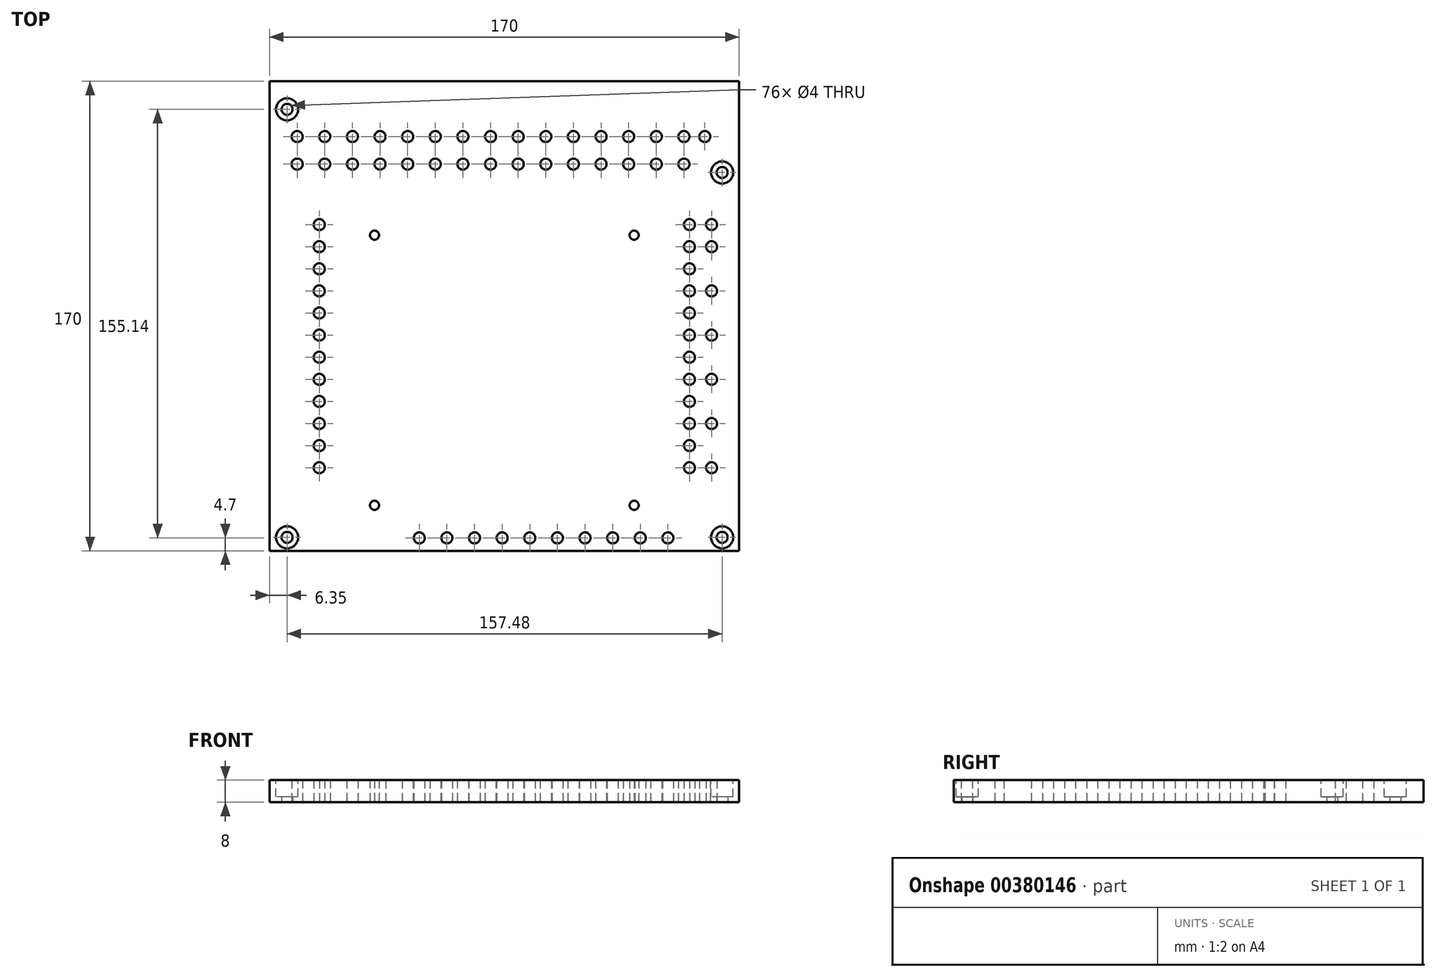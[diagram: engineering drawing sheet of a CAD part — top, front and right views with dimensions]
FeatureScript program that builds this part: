
annotation { "Feature Type Name" : "Feature", "Feature Type Description" : "" }
export const myFeature = defineFeature(function(context is Context, id is Id, definition is map)
    precondition{}
    {
        {
            var Q0;
            Q0=qCreatedBy(makeId("Top.planeOp"),FACE);
            var sketch = newSketch(context, id + "F0", { "sketchPlane" : qUnion([Q0])});
            skLineSegment(sketch, "E0.bottom", {"start": v(0, 0) * mm, "end": v(170, 0) * mm});
            skLineSegment(sketch, "E0.top", {"start": v(0, -170) * mm, "end": v(170, -170) * mm});
            skLineSegment(sketch, "E0.left", {"start": v(0, 0) * mm, "end": v(0, -170) * mm});
            skLineSegment(sketch, "E0.right", {"start": v(170, 0) * mm, "end": v(170, -170) * mm});
            skCircle(sketch, "E1", {"center": v(6.35, -10.16) * mm, "radius": 2 * mm});
            skCircle(sketch, "E2", {"center": v(163.83, -165.1) * mm, "radius": 2 * mm});
            skCircle(sketch, "E3", {"center": v(6.35, -165.1) * mm, "radius": 2 * mm});
            skCircle(sketch, "E4", {"center": v(163.83, -33.02) * mm, "radius": 2 * mm});
            skLineSegment(sketch, "E5.bottom", {"start": v(34.2, -51.9) * mm, "end": v(135.8, -51.9) * mm, "construction": true});
            skLineSegment(sketch, "E5.top", {"start": v(34.2, -157.3) * mm, "end": v(135.8, -157.3) * mm, "construction": true});
            skLineSegment(sketch, "E5.left", {"start": v(34.2, -51.89) * mm, "end": v(34.2, -157.3) * mm, "construction": true});
            skLineSegment(sketch, "E5.right", {"start": v(135.8, -51.89) * mm, "end": v(135.8, -157.3) * mm, "construction": true});
            skCircle(sketch, "E6", {"center": v(38, -55.7) * mm, "radius": 1.65 * mm});
            skLineSegment(sketch, "E7", {"start": v(85, -51.89) * mm, "end": v(85, -73.54) * mm, "construction": true});
            skLineSegment(sketch, "E8", {"start": v(34.2, -104.6) * mm, "end": v(74.49, -104.6) * mm, "construction": true});
            skCircle(sketch, "E9.MirrorC", {"center": v(38.01, -153.5) * mm, "radius": 1.65 * mm});
            skCircle(sketch, "E10.MirrorC", {"center": v(132, -55.7) * mm, "radius": 1.65 * mm});
            skCircle(sketch, "E11.MirrorC", {"center": v(132, -153.5) * mm, "radius": 1.65 * mm});
            skLineSegment(sketch, "E12", {"start": v(0, -85) * mm, "end": v(12.23, -85) * mm, "construction": true});
            skLineSegment(sketch, "E13", {"start": v(85, -170) * mm, "end": v(85, -151.97) * mm, "construction": true});
            skText(sketch, "E14", { "text": "Motors", "fontName": "OpenSans-Regular.ttf"});
            skText(sketch, "E15", { "text": "backside", "fontName": "OpenSans-Regular.ttf"});
            skText(sketch, "E16", { "text": "limit switches\n", "fontName": "OpenSans-Regular.ttf"});
            skLineSegment(sketch, "E17", {"start": v(18, -51.89) * mm, "end": v(18, -125.95) * mm, "construction": true});
            skCircle(sketch, "E18", {"center": v(18, -51.89) * mm, "radius": 2 * mm});
            skText(sketch, "E19", { "text": "USB", "fontName": "OpenSans-Regular.ttf"});
            skText(sketch, "E20", { "text": "24V", "fontName": "OpenSans-Regular.ttf"});
            skCircle(sketch, "E21.0.1.0", {"center": v(18, -59.89) * mm, "radius": 2 * mm});
            skCircle(sketch, "E21.0.2.0", {"center": v(18, -67.89) * mm, "radius": 2 * mm});
            skCircle(sketch, "E21.0.3.0", {"center": v(18, -75.89) * mm, "radius": 2 * mm});
            skCircle(sketch, "E21.0.4.0", {"center": v(18, -83.89) * mm, "radius": 2 * mm});
            skCircle(sketch, "E21.0.5.0", {"center": v(18, -91.89) * mm, "radius": 2 * mm});
            skCircle(sketch, "E21.0.6.0", {"center": v(18, -99.89) * mm, "radius": 2 * mm});
            skCircle(sketch, "E21.0.7.0", {"center": v(18, -107.89) * mm, "radius": 2 * mm});
            skLineSegment(sketch, "E21.direction1", {"start": v(18, -51.9) * mm, "end": v(9.88, -51.9) * mm, "construction": true});
            skLineSegment(sketch, "E21.direction2", {"start": v(18, -51.89) * mm, "end": v(18, -59.89) * mm, "construction": true});
            skCircle(sketch, "E22.0.0.8", {"center": v(18, -115.89) * mm, "radius": 2 * mm});
            skCircle(sketch, "E22.0.0.9", {"center": v(18, -123.89) * mm, "radius": 2 * mm});
            skCircle(sketch, "E22.0.0.10", {"center": v(18, -131.89) * mm, "radius": 2 * mm});
            skCircle(sketch, "E22.0.0.11", {"center": v(18, -139.89) * mm, "radius": 2 * mm});
            skCircle(sketch, "E23", {"center": v(10, -20) * mm, "radius": 2 * mm});
            skCircle(sketch, "E24.14.0.0", {"center": v(157.56, -20) * mm, "radius": 2 * mm});
            skCircle(sketch, "E25.0.1.0", {"center": v(10, -30) * mm, "radius": 2 * mm});
            skCircle(sketch, "E25.1.0.0", {"center": v(20, -20) * mm, "radius": 2 * mm});
            skCircle(sketch, "E25.1.1.0", {"center": v(20, -30) * mm, "radius": 2 * mm});
            skCircle(sketch, "E25.2.0.0", {"center": v(30, -20) * mm, "radius": 2 * mm});
            skCircle(sketch, "E25.2.1.0", {"center": v(30, -30) * mm, "radius": 2 * mm});
            skCircle(sketch, "E25.3.0.0", {"center": v(40, -20) * mm, "radius": 2 * mm});
            skCircle(sketch, "E25.3.1.0", {"center": v(40, -30) * mm, "radius": 2 * mm});
            skCircle(sketch, "E25.4.0.0", {"center": v(50, -20) * mm, "radius": 2 * mm});
            skCircle(sketch, "E25.4.1.0", {"center": v(50, -30) * mm, "radius": 2 * mm});
            skCircle(sketch, "E25.5.0.0", {"center": v(60, -20) * mm, "radius": 2 * mm});
            skCircle(sketch, "E25.5.1.0", {"center": v(60, -30) * mm, "radius": 2 * mm});
            skCircle(sketch, "E25.6.0.0", {"center": v(70, -20) * mm, "radius": 2 * mm});
            skCircle(sketch, "E25.6.1.0", {"center": v(70, -30) * mm, "radius": 2 * mm});
            skCircle(sketch, "E25.7.0.0", {"center": v(80, -20) * mm, "radius": 2 * mm});
            skCircle(sketch, "E25.7.1.0", {"center": v(80, -30) * mm, "radius": 2 * mm});
            skCircle(sketch, "E25.8.0.0", {"center": v(90, -20) * mm, "radius": 2 * mm});
            skCircle(sketch, "E25.8.1.0", {"center": v(90, -30) * mm, "radius": 2 * mm});
            skCircle(sketch, "E25.9.0.0", {"center": v(100, -20) * mm, "radius": 2 * mm});
            skCircle(sketch, "E25.9.1.0", {"center": v(100, -30) * mm, "radius": 2 * mm});
            skCircle(sketch, "E25.10.0.0", {"center": v(110, -20) * mm, "radius": 2 * mm});
            skCircle(sketch, "E25.10.1.0", {"center": v(110, -30) * mm, "radius": 2 * mm});
            skCircle(sketch, "E25.11.0.0", {"center": v(120, -20) * mm, "radius": 2 * mm});
            skCircle(sketch, "E25.11.1.0", {"center": v(120, -30) * mm, "radius": 2 * mm});
            skCircle(sketch, "E25.12.0.0", {"center": v(130, -20) * mm, "radius": 2 * mm});
            skCircle(sketch, "E25.12.1.0", {"center": v(130, -30) * mm, "radius": 2 * mm});
            skCircle(sketch, "E25.13.0.0", {"center": v(140, -20) * mm, "radius": 2 * mm});
            skCircle(sketch, "E25.13.1.0", {"center": v(140, -30) * mm, "radius": 2 * mm});
            skCircle(sketch, "E25.14.0.0", {"center": v(150, -20) * mm, "radius": 2 * mm});
            skCircle(sketch, "E25.14.1.0", {"center": v(150, -30) * mm, "radius": 2 * mm});
            skLineSegment(sketch, "E25.direction1", {"start": v(10, -20) * mm, "end": v(20, -20) * mm, "construction": true});
            skLineSegment(sketch, "E25.direction2", {"start": v(10, -20) * mm, "end": v(10, -30) * mm, "construction": true});
            skLineSegment(sketch, "E26", {"start": v(150, -20) * mm, "end": v(10, -20) * mm, "construction": true});
            skLineSegment(sketch, "E27", {"start": v(152, -51.9) * mm, "end": v(152, -141.8) * mm, "construction": true});
            skCircle(sketch, "E28", {"center": v(152, -51.9) * mm, "radius": 2 * mm});
            skCircle(sketch, "E29.0.1.0", {"center": v(152, -59.89) * mm, "radius": 2 * mm});
            skCircle(sketch, "E29.0.2.0", {"center": v(152, -67.89) * mm, "radius": 2 * mm});
            skCircle(sketch, "E29.0.3.0", {"center": v(152, -75.89) * mm, "radius": 2 * mm});
            skCircle(sketch, "E29.0.4.0", {"center": v(152, -83.89) * mm, "radius": 2 * mm});
            skCircle(sketch, "E29.0.5.0", {"center": v(152, -91.89) * mm, "radius": 2 * mm});
            skCircle(sketch, "E29.0.6.0", {"center": v(152, -99.89) * mm, "radius": 2 * mm});
            skCircle(sketch, "E29.0.7.0", {"center": v(152, -107.89) * mm, "radius": 2 * mm});
            skCircle(sketch, "E29.0.8.0", {"center": v(152, -115.89) * mm, "radius": 2 * mm});
            skCircle(sketch, "E29.0.9.0", {"center": v(152, -123.89) * mm, "radius": 2 * mm});
            skCircle(sketch, "E29.0.10.0", {"center": v(152, -131.89) * mm, "radius": 2 * mm});
            skCircle(sketch, "E29.0.11.0", {"center": v(152, -139.89) * mm, "radius": 2 * mm});
            skLineSegment(sketch, "E29.direction1", {"start": v(152, -51.9) * mm, "end": v(185.4, -51.9) * mm, "construction": true});
            skLineSegment(sketch, "E29.direction2", {"start": v(152, -51.9) * mm, "end": v(152, -59.89) * mm, "construction": true});
            skLineSegment(sketch, "E30", {"start": v(54.2, -165.3) * mm, "end": v(143.36, -165.3) * mm, "construction": true});
            skCircle(sketch, "E31", {"center": v(54.2, -165.3) * mm, "radius": 2 * mm});
            skCircle(sketch, "E32.1.0.0", {"center": v(64.2, -165.3) * mm, "radius": 2 * mm});
            skCircle(sketch, "E32.2.0.0", {"center": v(74.2, -165.3) * mm, "radius": 2 * mm});
            skCircle(sketch, "E32.3.0.0", {"center": v(84.2, -165.3) * mm, "radius": 2 * mm});
            skCircle(sketch, "E32.4.0.0", {"center": v(94.2, -165.3) * mm, "radius": 2 * mm});
            skCircle(sketch, "E32.5.0.0", {"center": v(104.2, -165.3) * mm, "radius": 2 * mm});
            skCircle(sketch, "E32.6.0.0", {"center": v(114.2, -165.3) * mm, "radius": 2 * mm});
            skCircle(sketch, "E32.7.0.0", {"center": v(124.2, -165.3) * mm, "radius": 2 * mm});
            skCircle(sketch, "E32.8.0.0", {"center": v(134.2, -165.3) * mm, "radius": 2 * mm});
            skCircle(sketch, "E32.9.0.0", {"center": v(144.2, -165.3) * mm, "radius": 2 * mm});
            skLineSegment(sketch, "E32.direction1", {"start": v(54.2, -165.3) * mm, "end": v(64.2, -165.3) * mm, "construction": true});
            skCircle(sketch, "E33", {"center": v(160, -51.9) * mm, "radius": 2 * mm});
            skCircle(sketch, "E34", {"center": v(160, -139.89) * mm, "radius": 2 * mm});
            skLineSegment(sketch, "E35", {"start": v(152, -139.89) * mm, "end": v(160, -139.89) * mm, "construction": true});
            skLineSegment(sketch, "E36", {"start": v(160, -139.89) * mm, "end": v(160, -107.89) * mm, "construction": true});
            skCircle(sketch, "E37", {"center": v(160, -123.89) * mm, "radius": 2 * mm});
            skLineSegment(sketch, "E38", {"start": v(152, -123.89) * mm, "end": v(160, -123.89) * mm, "construction": true});
            skCircle(sketch, "E39", {"center": v(160, -107.89) * mm, "radius": 2 * mm});
            skLineSegment(sketch, "E40", {"start": v(152, -107.89) * mm, "end": v(160, -107.89) * mm, "construction": true});
            skLineSegment(sketch, "E41", {"start": v(160, -107.89) * mm, "end": v(160, -51.9) * mm, "construction": true});
            skCircle(sketch, "E42", {"center": v(160, -91.89) * mm, "radius": 2 * mm});
            skCircle(sketch, "E43", {"center": v(160, -75.89) * mm, "radius": 2 * mm});
            skCircle(sketch, "E44", {"center": v(160, -59.89) * mm, "radius": 2 * mm});
            skLineSegment(sketch, "E45", {"start": v(160, -91.89) * mm, "end": v(152, -91.89) * mm, "construction": true});
            skLineSegment(sketch, "E46", {"start": v(160, -75.89) * mm, "end": v(152, -75.89) * mm, "construction": true});
            skLineSegment(sketch, "E47", {"start": v(160, -59.89) * mm, "end": v(152, -59.89) * mm, "construction": true});
            const initialGuessF0  = {"E14": [-0.03435, -0.08895, 1, 0, 0.00543], "E15": [0.04294, 0.00804, 1, 0, 0.00895], "E16": [0.17197, -0.0727, 1, 0, 0.0029], "E19": [0.09725, 0.0018, 1, 0, 0.00662], "E20": [0.0422, -0.18058, 1, 0, 0.00788]};
            skSetInitialGuess(sketch, initialGuessF0);
            skSolve(sketch);
        }
        {
            var Q0;
            Q0=makeQuery(id+"F0.imprint","IMPRINT",FACE,{"disambiguationData":[TD([[makeQuery(id+"F0.imprint","IMPRINT",EDGE,{"derivedFrom":sQuery(id+"F0.wireOp",EDGE,"E0.bottom")}),-1.0]])]});
            extrude(context, id + "F1", {"entities" : qUnion([Q0]), "depth" : 8 * mm});
        }
        {
            var Q0;
            Q0=makeQuery(id+"F1.opExtrude","CAP_FACE",FACE,{"disambiguationData":[OSD([sQuery(id+"F0.wireOp",EDGE,"E0.bottom"),sQuery(id+"F0.wireOp",EDGE,"E0.top"),sQuery(id+"F0.wireOp",EDGE,"E0.left"),sQuery(id+"F0.wireOp",EDGE,"E0.right"),sQuery(id+"F0.wireOp",EDGE,"E1"),sQuery(id+"F0.wireOp",EDGE,"E2"),sQuery(id+"F0.wireOp",EDGE,"E3"),sQuery(id+"F0.wireOp",EDGE,"E4"),sQuery(id+"F0.wireOp",EDGE,"E6"),sQuery(id+"F0.wireOp",EDGE,"E9.MirrorC"),sQuery(id+"F0.wireOp",EDGE,"E10.MirrorC"),sQuery(id+"F0.wireOp",EDGE,"E11.MirrorC"),sQuery(id+"F0.wireOp",EDGE,"E18"),sQuery(id+"F0.wireOp",EDGE,"E21.0.1.0"),sQuery(id+"F0.wireOp",EDGE,"E21.0.2.0"),sQuery(id+"F0.wireOp",EDGE,"E21.0.3.0"),sQuery(id+"F0.wireOp",EDGE,"E21.0.4.0"),sQuery(id+"F0.wireOp",EDGE,"E21.0.5.0"),sQuery(id+"F0.wireOp",EDGE,"E21.0.6.0"),sQuery(id+"F0.wireOp",EDGE,"E21.0.7.0"),sQuery(id+"F0.wireOp",EDGE,"E22.0.0.8"),sQuery(id+"F0.wireOp",EDGE,"E22.0.0.9"),sQuery(id+"F0.wireOp",EDGE,"E22.0.0.10"),sQuery(id+"F0.wireOp",EDGE,"E22.0.0.11"),sQuery(id+"F0.wireOp",EDGE,"E23"),sQuery(id+"F0.wireOp",EDGE,"E24.14.0.0"),sQuery(id+"F0.wireOp",EDGE,"E25.0.1.0"),sQuery(id+"F0.wireOp",EDGE,"E25.1.0.0"),sQuery(id+"F0.wireOp",EDGE,"E25.1.1.0"),sQuery(id+"F0.wireOp",EDGE,"E25.2.0.0"),sQuery(id+"F0.wireOp",EDGE,"E25.2.1.0"),sQuery(id+"F0.wireOp",EDGE,"E25.3.0.0"),sQuery(id+"F0.wireOp",EDGE,"E25.3.1.0"),sQuery(id+"F0.wireOp",EDGE,"E25.4.0.0"),sQuery(id+"F0.wireOp",EDGE,"E25.4.1.0"),sQuery(id+"F0.wireOp",EDGE,"E25.5.0.0"),sQuery(id+"F0.wireOp",EDGE,"E25.5.1.0"),sQuery(id+"F0.wireOp",EDGE,"E25.6.0.0"),sQuery(id+"F0.wireOp",EDGE,"E25.6.1.0"),sQuery(id+"F0.wireOp",EDGE,"E25.7.0.0"),sQuery(id+"F0.wireOp",EDGE,"E25.7.1.0"),sQuery(id+"F0.wireOp",EDGE,"E25.8.0.0"),sQuery(id+"F0.wireOp",EDGE,"E25.8.1.0"),sQuery(id+"F0.wireOp",EDGE,"E25.9.0.0"),sQuery(id+"F0.wireOp",EDGE,"E25.9.1.0"),sQuery(id+"F0.wireOp",EDGE,"E25.10.0.0"),sQuery(id+"F0.wireOp",EDGE,"E25.10.1.0"),sQuery(id+"F0.wireOp",EDGE,"E25.11.0.0"),sQuery(id+"F0.wireOp",EDGE,"E25.11.1.0"),sQuery(id+"F0.wireOp",EDGE,"E25.12.0.0"),sQuery(id+"F0.wireOp",EDGE,"E25.12.1.0"),sQuery(id+"F0.wireOp",EDGE,"E25.13.0.0"),sQuery(id+"F0.wireOp",EDGE,"E25.13.1.0"),sQuery(id+"F0.wireOp",EDGE,"E25.14.0.0"),sQuery(id+"F0.wireOp",EDGE,"E25.14.1.0"),sQuery(id+"F0.wireOp",EDGE,"E28"),sQuery(id+"F0.wireOp",EDGE,"E29.0.1.0"),sQuery(id+"F0.wireOp",EDGE,"E29.0.2.0"),sQuery(id+"F0.wireOp",EDGE,"E29.0.3.0"),sQuery(id+"F0.wireOp",EDGE,"E29.0.4.0"),sQuery(id+"F0.wireOp",EDGE,"E29.0.5.0"),sQuery(id+"F0.wireOp",EDGE,"E29.0.6.0"),sQuery(id+"F0.wireOp",EDGE,"E29.0.7.0"),sQuery(id+"F0.wireOp",EDGE,"E29.0.8.0"),sQuery(id+"F0.wireOp",EDGE,"E29.0.9.0"),sQuery(id+"F0.wireOp",EDGE,"E29.0.10.0"),sQuery(id+"F0.wireOp",EDGE,"E29.0.11.0"),sQuery(id+"F0.wireOp",EDGE,"E31"),sQuery(id+"F0.wireOp",EDGE,"E32.1.0.0"),sQuery(id+"F0.wireOp",EDGE,"E32.2.0.0"),sQuery(id+"F0.wireOp",EDGE,"E32.3.0.0"),sQuery(id+"F0.wireOp",EDGE,"E32.4.0.0"),sQuery(id+"F0.wireOp",EDGE,"E32.5.0.0"),sQuery(id+"F0.wireOp",EDGE,"E32.6.0.0"),sQuery(id+"F0.wireOp",EDGE,"E32.7.0.0"),sQuery(id+"F0.wireOp",EDGE,"E32.8.0.0"),sQuery(id+"F0.wireOp",EDGE,"E32.9.0.0"),sQuery(id+"F0.wireOp",EDGE,"E33"),sQuery(id+"F0.wireOp",EDGE,"E34"),sQuery(id+"F0.wireOp",EDGE,"E37"),sQuery(id+"F0.wireOp",EDGE,"E39"),sQuery(id+"F0.wireOp",EDGE,"E42"),sQuery(id+"F0.wireOp",EDGE,"E43"),sQuery(id+"F0.wireOp",EDGE,"E44")])],"isStart":false});
            var sketch = newSketch(context, id + "F2", { "sketchPlane" : qUnion([Q0])});
            skCircle(sketch, "E48", {"center": v(6.35, -10.16) * mm, "radius": 4 * mm});
            skCircle(sketch, "E49", {"center": v(163.83, -33.02) * mm, "radius": 4 * mm});
            skCircle(sketch, "E50", {"center": v(163.83, -165.1) * mm, "radius": 4 * mm});
            skCircle(sketch, "E51", {"center": v(6.35, -165.1) * mm, "radius": 4 * mm});
            skSolve(sketch);
        }
        {
            var Q0;
            Q0=makeQuery(id+"F2.imprint","IMPRINT",FACE,{"disambiguationData":[TD([[makeQuery(id+"F2.imprint","IMPRINT",EDGE,{"derivedFrom":sQuery(id+"F2.wireOp",EDGE,"E49")}),1.0]])]});
            var Q1;
            Q1=makeQuery(id+"F2.imprint","IMPRINT",FACE,{"disambiguationData":[TD([[makeQuery(id+"F2.imprint","IMPRINT",EDGE,{"derivedFrom":sQuery(id+"F2.wireOp",EDGE,"E50")}),1.0]])]});
            var Q2;
            Q2=makeQuery(id+"F2.imprint","IMPRINT",FACE,{"disambiguationData":[TD([[makeQuery(id+"F2.imprint","IMPRINT",EDGE,{"derivedFrom":sQuery(id+"F2.wireOp",EDGE,"E51")}),1.0]])]});
            var Q3;
            Q3=makeQuery(id+"F2.imprint","IMPRINT",FACE,{"disambiguationData":[TD([[makeQuery(id+"F2.imprint","IMPRINT",EDGE,{"derivedFrom":sQuery(id+"F2.wireOp",EDGE,"E48")}),1.0]])]});
            extrude(context, id + "F3", {"entities" : qUnion([Q0, Q1, Q2, Q3]), "operationType" : NewBodyOperationType.REMOVE, "oppositeDirection" : true, "depth" : 6 * mm});
        }
    });
